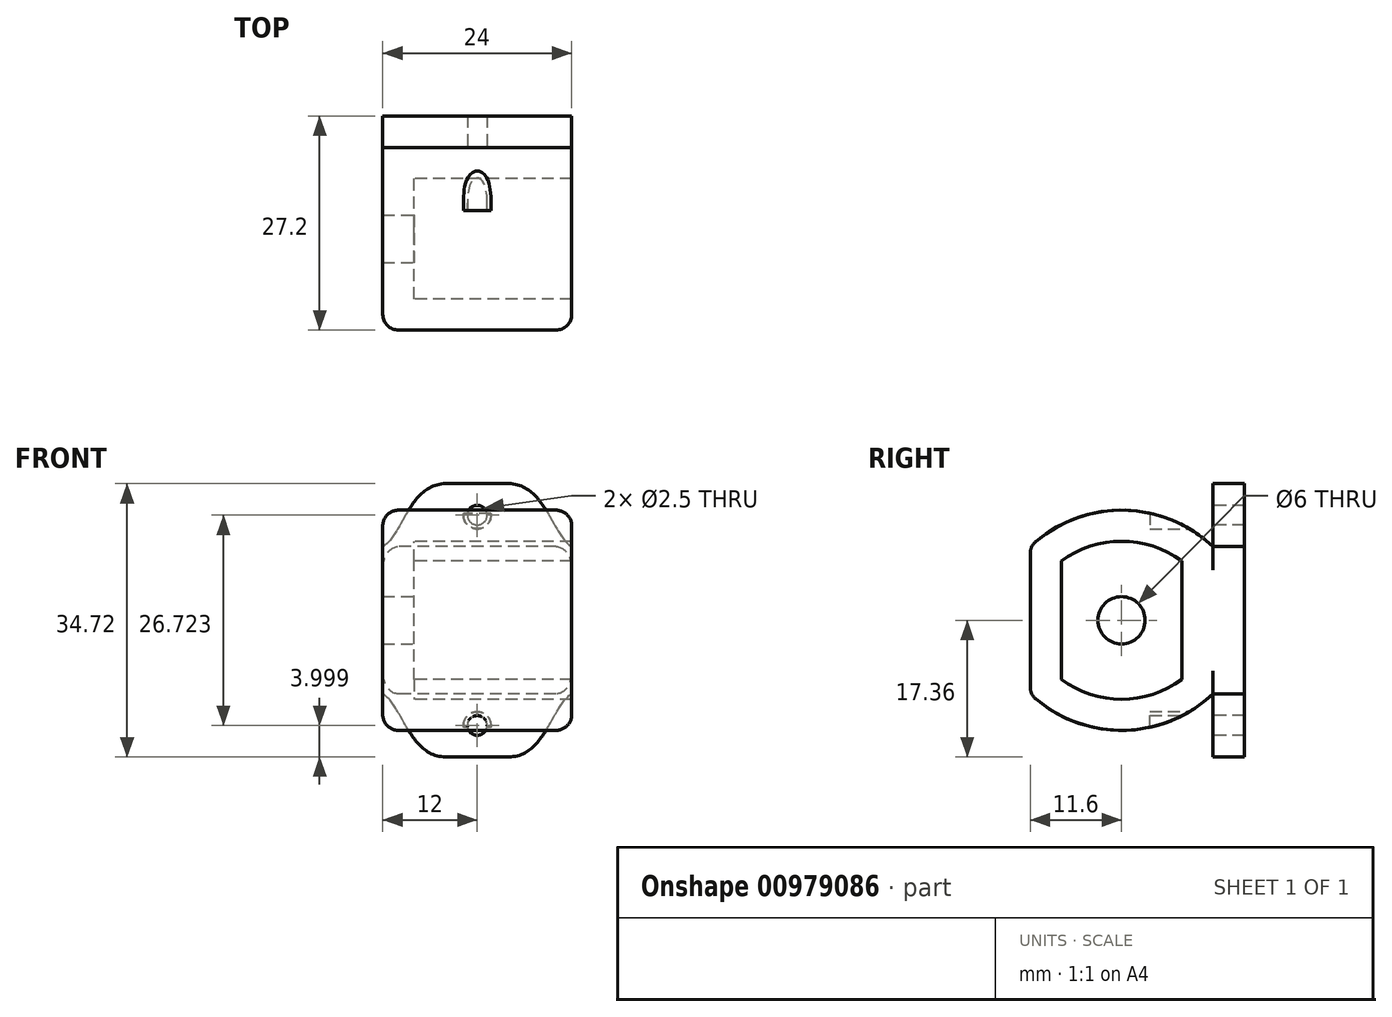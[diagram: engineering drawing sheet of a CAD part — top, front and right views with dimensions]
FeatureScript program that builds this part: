
annotation { "Feature Type Name" : "Feature", "Feature Type Description" : "" }
export const myFeature = defineFeature(function(context is Context, id is Id, definition is map)
    precondition{}
    {
        {
            var Q0;
            Q0=qCreatedBy(makeId("Right.planeOp"),FACE);
            var sketch = newSketch(context, id + "F0", { "sketchPlane" : qUnion([Q0])});
            skPoint(sketch, "E0.middle", {"position": v(0, 0) * mm});
            skArc(sketch, "E1", {"start": v(7.6, 7.5) * mm, "mid": v(0, 9.99) * mm, "end": v(-7.6, 7.5) * mm});
            skArc(sketch, "E2.MirrorCS", {"start": v(7.6, -7.5) * mm, "mid": v(0, -9.99) * mm, "end": v(-7.6, -7.5) * mm});
            skLineSegment(sketch, "E3", {"start": v(-7.6, 7.5) * mm, "end": v(-7.6, -7.5) * mm});
            skLineSegment(sketch, "E4", {"start": v(7.6, -7.5) * mm, "end": v(7.6, 7.5) * mm});
            skLineSegment(sketch, "E5.0", {"start": v(-11.6, 9.36) * mm, "end": v(-11.6, -9.36) * mm});
            skArc(sketch, "E5.1", {"start": v(11.6, 9.36) * mm, "mid": v(0, 13.99) * mm, "end": v(-11.6, 9.36) * mm});
            skLineSegment(sketch, "E5.2", {"start": v(11.6, -9.36) * mm, "end": v(11.6, 9.36) * mm});
            skArc(sketch, "E5.3", {"start": v(11.6, -9.36) * mm, "mid": v(0, -13.99) * mm, "end": v(-11.6, -9.36) * mm});
            skCircle(sketch, "E6", {"center": v(0, 0) * mm, "radius": 3 * mm});
            skLineSegment(sketch, "E7.0", {"start": v(7.65, -7.53) * mm, "end": v(7.65, 7.53) * mm});
            skArc(sketch, "E7.1", {"start": v(7.65, -7.53) * mm, "mid": v(0, -10.04) * mm, "end": v(-7.65, -7.53) * mm});
            skLineSegment(sketch, "E7.2", {"start": v(-7.65, 7.53) * mm, "end": v(-7.65, -7.53) * mm});
            skArc(sketch, "E7.3", {"start": v(7.65, 7.53) * mm, "mid": v(0, 10.04) * mm, "end": v(-7.65, 7.53) * mm});
            skSolve(sketch);
        }
        {
            var Q0;
            Q0 = qSketchRegion(id + "F0", true);
            extrude(context, id + "F1", {"entities" : qUnion([Q0]), "depth" : 20 * mm, "offsetDistance" : 25 * mm});
        }
        {
            var Q0;
            Q0=makeQuery(id+"F0.imprint","IMPRINT",FACE,{"disambiguationData":[TD([[makeQuery(id+"F0.imprint","IMPRINT",EDGE,{"derivedFrom":sQuery(id+"F0.wireOp",EDGE,"E1")}),1.0]])]});
            var Q1;
            Q1=makeQuery(id+"F0.imprint","IMPRINT",FACE,{"disambiguationData":[TD([[makeQuery(id+"F0.imprint","IMPRINT",EDGE,{"derivedFrom":sQuery(id+"F0.wireOp",EDGE,"E1")}),-1.0]])]});
            var Q2;
            Q2=makeQuery(id+"F0.imprint","IMPRINT",FACE,{"disambiguationData":[TD([[makeQuery(id+"F0.imprint","IMPRINT",EDGE,{"derivedFrom":sQuery(id+"F0.wireOp",EDGE,"E5.0")}),1.0]])]});
            extrude(context, id + "F2", {"entities" : qUnion([Q0, Q1, Q2]), "operationType" : NewBodyOperationType.ADD, "depth" : -4 * mm, "offsetDistance" : 25 * mm});
        }
        {
            var Q0;
            {var subQ0=sQuery(id+"F0.wireOp",EDGE,"E5.2");Q0=makeQuery(id+"F2.boolean.opBoolean","MERGE",FACE,{"derivedFrom":[makeQuery(id+"F1.opExtrude","SWEPT_FACE",FACE,{"disambiguationData":[OSD([subQ0])]}),makeQuery(id+"F2.opExtrude","SWEPT_FACE",FACE,{"disambiguationData":[OSD([subQ0])]})]});}
            var sketch = newSketch(context, id + "F3", { "sketchPlane" : qUnion([Q0])});
            skLineSegment(sketch, "E8.bottom", {"start": v(-4, 17.36) * mm, "end": v(-12, 17.36) * mm});
            skPoint(sketch, "E8.middle", {"position": v(-8, 9.36) * mm});
            skLineSegment(sketch, "E9", {"start": v(-4, 17.36) * mm, "end": v(-4, 9.36) * mm});
            skLineSegment(sketch, "E10", {"start": v(-12, 17.36) * mm, "end": v(-12, 9.36) * mm});
            skLineSegment(sketch, "E11", {"start": v(-12, 9.36) * mm, "end": v(-4, 9.36) * mm});
            skCircle(sketch, "E12", {"center": v(-8, 13.36) * mm, "radius": 1.25 * mm});
            skPoint(sketch, "E12.centerSnap0", {"position": v(-4, 13.36) * mm});
            skPoint(sketch, "E13.MirrorP", {"position": v(-4, -13.36) * mm});
            skLineSegment(sketch, "E14.MirrorCS", {"start": v(-4, -17.36) * mm, "end": v(-12, -17.36) * mm});
            skLineSegment(sketch, "E15.MirrorCS", {"start": v(-12, -9.36) * mm, "end": v(-4, -9.36) * mm});
            skLineSegment(sketch, "E16.MirrorCS", {"start": v(-12, -17.36) * mm, "end": v(-12, -9.36) * mm});
            skLineSegment(sketch, "E17.MirrorCS", {"start": v(-4, -17.36) * mm, "end": v(-4, -9.36) * mm});
            skCircle(sketch, "E18.MirrorC", {"center": v(-8, -13.36) * mm, "radius": 1.25 * mm});
            skPoint(sketch, "E19.MirrorP", {"position": v(-8, -9.36) * mm});
            skFitSpline(sketch, "E20", {"points": [v(-4, -17.36) * mm, v(4, -9.36) * mm, v(13.83, -14.24) * mm], "startDerivative": vector(27.43, 0.2) * mm, "endDerivative": vector(20.78, -16.21) * mm});
            skFitSpline(sketch, "E21.MirrorCS", {"points": [v(-12, -17.36) * mm, v(-20, -9.36) * mm, v(-29.83, -14.24) * mm], "startDerivative": vector(-27.43, 0.2) * mm, "endDerivative": vector(-20.78, -16.21) * mm});
            skFitSpline(sketch, "E22.MirrorCS", {"points": [v(-4, -17.36) * mm, v(4, -9.36) * mm, v(13.83, -14.24) * mm], "startDerivative": vector(27.43, 0.2) * mm, "endDerivative": vector(20.78, -16.21) * mm});
            skFitSpline(sketch, "E23.MirrorCS", {"points": [v(-4, 17.36) * mm, v(4, 9.36) * mm, v(13.83, 14.24) * mm], "startDerivative": vector(27.43, -0.2) * mm, "endDerivative": vector(20.78, 16.21) * mm});
            skFitSpline(sketch, "E24.MirrorCS", {"points": [v(-12, 17.36) * mm, v(-20, 9.36) * mm, v(-29.83, 14.24) * mm], "startDerivative": vector(-27.43, -0.2) * mm, "endDerivative": vector(-20.78, 16.21) * mm});
            skSolve(sketch);
        }
        {
            var Q0;
            Q0=makeQuery(id+"F3.imprint","IMPRINT",FACE,{"disambiguationData":[TD([[makeQuery(id+"F3.imprint","IMPRINT",EDGE,{"derivedFrom":sQuery(id+"F3.wireOp",EDGE,"E8.bottom")}),1.0]])]});
            var Q1;
            Q1=makeQuery(id+"F3.imprint","IMPRINT",FACE,{"disambiguationData":[TD([[makeQuery(id+"F3.imprint","IMPRINT",EDGE,{"derivedFrom":sQuery(id+"F3.wireOp",EDGE,"E14.MirrorCS")}),-1.0]])]});
            var Q2;
            {var subQ4=sQuery(id+"F3.wireOp",EDGE,"E11");Q2=makeQuery(id+"F3.imprint","IMPRINT",FACE,{"disambiguationData":[TD([[makeQuery(id+"F3.imprint","IMPRINT",EDGE,{"derivedFrom":subQ4}),-1.0]])]});}
            var Q3;
            {var subQ0=sQuery(id+"F3.wireOp",EDGE,"E10");Q3=makeQuery(id+"F3.imprint","IMPRINT",FACE,{"disambiguationData":[TD([[makeQuery(id+"F3.imprint","IMPRINT",EDGE,{"derivedFrom":subQ0}),-1.0]])]});}
            var Q4;
            {var subQ0=sQuery(id+"F3.wireOp",EDGE,"E9");Q4=makeQuery(id+"F3.imprint","IMPRINT",FACE,{"disambiguationData":[TD([[makeQuery(id+"F3.imprint","IMPRINT",EDGE,{"derivedFrom":subQ0}),1.0]])]});}
            var Q5;
            {var subQ0=sQuery(id+"F3.wireOp",EDGE,"E17.MirrorCS");Q5=makeQuery(id+"F3.imprint","IMPRINT",FACE,{"disambiguationData":[TD([[makeQuery(id+"F3.imprint","IMPRINT",EDGE,{"derivedFrom":subQ0}),-1.0]])]});}
            var Q6;
            {var subQ0=sQuery(id+"F3.wireOp",EDGE,"E16.MirrorCS");Q6=makeQuery(id+"F3.imprint","IMPRINT",FACE,{"disambiguationData":[TD([[makeQuery(id+"F3.imprint","IMPRINT",EDGE,{"derivedFrom":subQ0}),1.0]])]});}
            extrude(context, id + "F4", {"entities" : qUnion([Q0, Q1, Q2, Q3, Q4, Q5, Q6]), "operationType" : NewBodyOperationType.ADD, "depth" : 4 * mm, "offsetDistance" : 25 * mm});
        }
        {
            var Q0;
            {var subQ0=sQuery(id+"F3.wireOp",EDGE,"E9");var subQ1=sQuery(id+"F3.wireOp",EDGE,"E8.bottom");var subQ2=sQuery(id+"F0.wireOp",EDGE,"E5.1");var subQ3=sQuery(id+"F3.wireOp",EDGE,"E10");var subQ4=sQuery(id+"F3.wireOp",EDGE,"E12");var subQ5=sQuery(id+"F0.wireOp",EDGE,"E5.2");Q0=makeQuery(id+"F4.boolean.opBoolean","SPLIT",FACE,{"disambiguationData":[TD([makeQuery(id+"F1.opExtrude","SWEPT_FACE",FACE,{"disambiguationData":[OSD([subQ2])]})])],"derivedFrom":makeQuery(id+"F4.opExtrude","CAP_FACE",FACE,{"disambiguationData":[OSD([subQ2,subQ5,sQuery(id+"F0.wireOp",EDGE,"E5.3"),subQ1,subQ0,subQ3,subQ4,sQuery(id+"F3.wireOp",EDGE,"E14.MirrorCS"),sQuery(id+"F3.wireOp",EDGE,"E16.MirrorCS"),sQuery(id+"F3.wireOp",EDGE,"E17.MirrorCS"),sQuery(id+"F3.wireOp",EDGE,"E18.MirrorC")])],"isStart":true})});}
            var sketch = newSketch(context, id + "F5", { "sketchPlane" : qUnion([Q0])});
            skCircle(sketch, "E25", {"center": v(8, 13.36) * mm, "radius": 1.75 * mm});
            skSolve(sketch);
        }
        {
            var Q0;
            {var subQ0=sQuery(id+"F3.wireOp",EDGE,"E16.MirrorCS");var subQ1=sQuery(id+"F3.wireOp",EDGE,"E14.MirrorCS");var subQ2=sQuery(id+"F0.wireOp",EDGE,"E5.3");var subQ3=sQuery(id+"F3.wireOp",EDGE,"E17.MirrorCS");var subQ4=sQuery(id+"F3.wireOp",EDGE,"E18.MirrorC");var subQ5=sQuery(id+"F0.wireOp",EDGE,"E5.2");Q0=makeQuery(id+"F4.boolean.opBoolean","SPLIT",FACE,{"disambiguationData":[TD([makeQuery(id+"F1.opExtrude","SWEPT_FACE",FACE,{"disambiguationData":[OSD([subQ2])]})])],"derivedFrom":makeQuery(id+"F4.opExtrude","CAP_FACE",FACE,{"disambiguationData":[OSD([sQuery(id+"F0.wireOp",EDGE,"E5.1"),subQ5,subQ2,sQuery(id+"F3.wireOp",EDGE,"E8.bottom"),sQuery(id+"F3.wireOp",EDGE,"E9"),sQuery(id+"F3.wireOp",EDGE,"E10"),sQuery(id+"F3.wireOp",EDGE,"E12"),subQ1,subQ0,subQ3,subQ4])],"isStart":true})});}
            var sketch = newSketch(context, id + "F6", { "sketchPlane" : qUnion([Q0])});
            skCircle(sketch, "E26", {"center": v(8, -13.36) * mm, "radius": 1.75 * mm});
            skSolve(sketch);
        }
        {
            var Q0;
            Q0=makeQuery(id+"F6.imprint","IMPRINT",FACE,{"disambiguationData":[TD([[makeQuery(id+"F6.imprint","IMPRINT",EDGE,{"derivedFrom":sQuery(id+"F6.wireOp",EDGE,"E26")}),1.0]])]});
            extrude(context, id + "F7", {"entities" : qUnion([Q0]), "operationType" : NewBodyOperationType.REMOVE, "depth" : 8 * mm, "offsetDistance" : 25 * mm});
        }
        {
            var Q0;
            Q0=makeQuery(id+"F2.opExtrude","CAP_EDGE",EDGE,{"disambiguationData":[OSD([sQuery(id+"F0.wireOp",EDGE,"E5.1")])],"isStart":false});
            var Q1;
            Q1=makeQuery(id+"F2.opExtrude","CAP_EDGE",EDGE,{"disambiguationData":[OSD([sQuery(id+"F0.wireOp",EDGE,"E5.0")])],"isStart":false});
            var Q2;
            Q2=makeQuery(id+"F2.opExtrude","CAP_EDGE",EDGE,{"disambiguationData":[OSD([sQuery(id+"F0.wireOp",EDGE,"E5.3")])],"isStart":false});
            var Q3;
            {var subQ0=sQuery(id+"F0.wireOp",EDGE,"E5.1");var subQ1=sQuery(id+"F0.wireOp",EDGE,"E5.0");Q3=makeQuery(id+"F2.boolean.opBoolean","MERGE",EDGE,{"derivedFrom":[makeQuery(id+"F1.opExtrude","SWEPT_EDGE",EDGE,{"disambiguationData":[OSD([subQ1,subQ0])]}),makeQuery(id+"F2.opExtrude","SWEPT_EDGE",EDGE,{"disambiguationData":[OSD([subQ1,subQ0])]})]});}
            var Q4;
            {var subQ0=sQuery(id+"F0.wireOp",EDGE,"E5.3");var subQ1=sQuery(id+"F0.wireOp",EDGE,"E5.0");Q4=makeQuery(id+"F2.boolean.opBoolean","MERGE",EDGE,{"derivedFrom":[makeQuery(id+"F1.opExtrude","SWEPT_EDGE",EDGE,{"disambiguationData":[OSD([subQ1,subQ0])]}),makeQuery(id+"F2.opExtrude","SWEPT_EDGE",EDGE,{"disambiguationData":[OSD([subQ1,subQ0])]})]});}
            var Q5;
            Q5=makeQuery(id+"F1.opExtrude","CAP_EDGE",EDGE,{"disambiguationData":[OSD([sQuery(id+"F0.wireOp",EDGE,"E5.0")])],"isStart":false});
            var Q6;
            Q6=makeQuery(id+"F1.opExtrude","CAP_EDGE",EDGE,{"disambiguationData":[OSD([sQuery(id+"F0.wireOp",EDGE,"E5.1")])],"isStart":false});
            var Q7;
            Q7=makeQuery(id+"F1.opExtrude","CAP_EDGE",EDGE,{"disambiguationData":[OSD([sQuery(id+"F0.wireOp",EDGE,"E5.3")])],"isStart":false});
            var Q8;
            {var subQ0=sQuery(id+"F3.wireOp",EDGE,"E17.MirrorCS");var subQ1=sQuery(id+"F3.wireOp",EDGE,"E14.MirrorCS");Q8=makeQuery(id+"FF6rtlHh2VJHCVL_1.boolean.opBoolean","MERGE",EDGE,{"derivedFrom":[makeQuery(id+"F4.opExtrude","SWEPT_EDGE",EDGE,{"disambiguationData":[OSD([subQ1,subQ0])]}),makeQuery(id+"FF6rtlHh2VJHCVL_1.opExtrude","SWEPT_EDGE",EDGE,{"disambiguationData":[OSD([subQ1,subQ0])]})]});}
            var Q9;
            {var subQ0=sQuery(id+"F3.wireOp",EDGE,"E16.MirrorCS");var subQ1=sQuery(id+"F3.wireOp",EDGE,"E14.MirrorCS");Q9=makeQuery(id+"FF6rtlHh2VJHCVL_1.boolean.opBoolean","MERGE",EDGE,{"derivedFrom":[makeQuery(id+"F4.opExtrude","SWEPT_EDGE",EDGE,{"disambiguationData":[OSD([subQ1,subQ0])]}),makeQuery(id+"FF6rtlHh2VJHCVL_1.opExtrude","SWEPT_EDGE",EDGE,{"disambiguationData":[OSD([subQ1,subQ0])]})]});}
            var Q10;
            {var subQ0=sQuery(id+"F3.wireOp",EDGE,"E10");var subQ1=sQuery(id+"F3.wireOp",EDGE,"E8.bottom");Q10=makeQuery(id+"Fi3vcruLf0SJVk7_1.boolean.opBoolean","MERGE",EDGE,{"derivedFrom":[makeQuery(id+"F4.opExtrude","SWEPT_EDGE",EDGE,{"disambiguationData":[OSD([subQ1,subQ0])]}),makeQuery(id+"Fi3vcruLf0SJVk7_1.opExtrude","SWEPT_EDGE",EDGE,{"disambiguationData":[OSD([subQ1,subQ0])]})]});}
            var Q11;
            {var subQ0=sQuery(id+"F3.wireOp",EDGE,"E9");var subQ1=sQuery(id+"F3.wireOp",EDGE,"E8.bottom");Q11=makeQuery(id+"Fi3vcruLf0SJVk7_1.boolean.opBoolean","MERGE",EDGE,{"derivedFrom":[makeQuery(id+"F4.opExtrude","SWEPT_EDGE",EDGE,{"disambiguationData":[OSD([subQ1,subQ0])]}),makeQuery(id+"Fi3vcruLf0SJVk7_1.opExtrude","SWEPT_EDGE",EDGE,{"disambiguationData":[OSD([subQ1,subQ0])]})]});}
            fillet(context, id + "F8", {"entities" : qUnion([Q0, Q1, Q2, Q3, Q4, Q5, Q6, Q7, Q8, Q9, Q10, Q11]), "radius" : 2 * mm, "tangentPropagation" : true, "allowEdgeOverflow" : false});
        }
        {
            var Q0;
            Q0=makeQuery(id+"F6.imprint","IMPRINT",FACE,{"disambiguationData":[TD([[makeQuery(id+"F6.imprint","IMPRINT",EDGE,{"derivedFrom":sQuery(id+"F6.wireOp",EDGE,"E26")}),1.0]])]});
            var Q1;
            Q1=makeQuery(id+"F6.imprint","IMPRINT",FACE,{"disambiguationData":[TD([[makeQuery(id+"F6.imprint","IMPRINT",EDGE,{"derivedFrom":makeQuery(id+"F4.opExtrude","CAP_EDGE",EDGE,{"disambiguationData":[OSD([sQuery(id+"F3.wireOp",EDGE,"E18.MirrorC")])],"isStart":true})}),1.0]])]});
            extrude(context, id + "F9", {"entities" : qUnion([Q0, Q1]), "operationType" : NewBodyOperationType.REMOVE, "depth" : 8 * mm, "offsetDistance" : 25 * mm});
        }
        {
            var Q0;
            Q0=makeQuery(id+"F5.imprint","IMPRINT",FACE,{"disambiguationData":[TD([[makeQuery(id+"F5.imprint","IMPRINT",EDGE,{"derivedFrom":makeQuery(id+"F4.opExtrude","CAP_EDGE",EDGE,{"disambiguationData":[OSD([sQuery(id+"F3.wireOp",EDGE,"E12")])],"isStart":true})}),-1.0]])]});
            var Q1;
            Q1=makeQuery(id+"F5.imprint","IMPRINT",FACE,{"disambiguationData":[TD([[makeQuery(id+"F5.imprint","IMPRINT",EDGE,{"derivedFrom":sQuery(id+"F5.wireOp",EDGE,"E25")}),1.0]])]});
            extrude(context, id + "F10", {"entities" : qUnion([Q0, Q1]), "operationType" : NewBodyOperationType.REMOVE, "depth" : 8 * mm, "offsetDistance" : 25 * mm});
        }
    });
